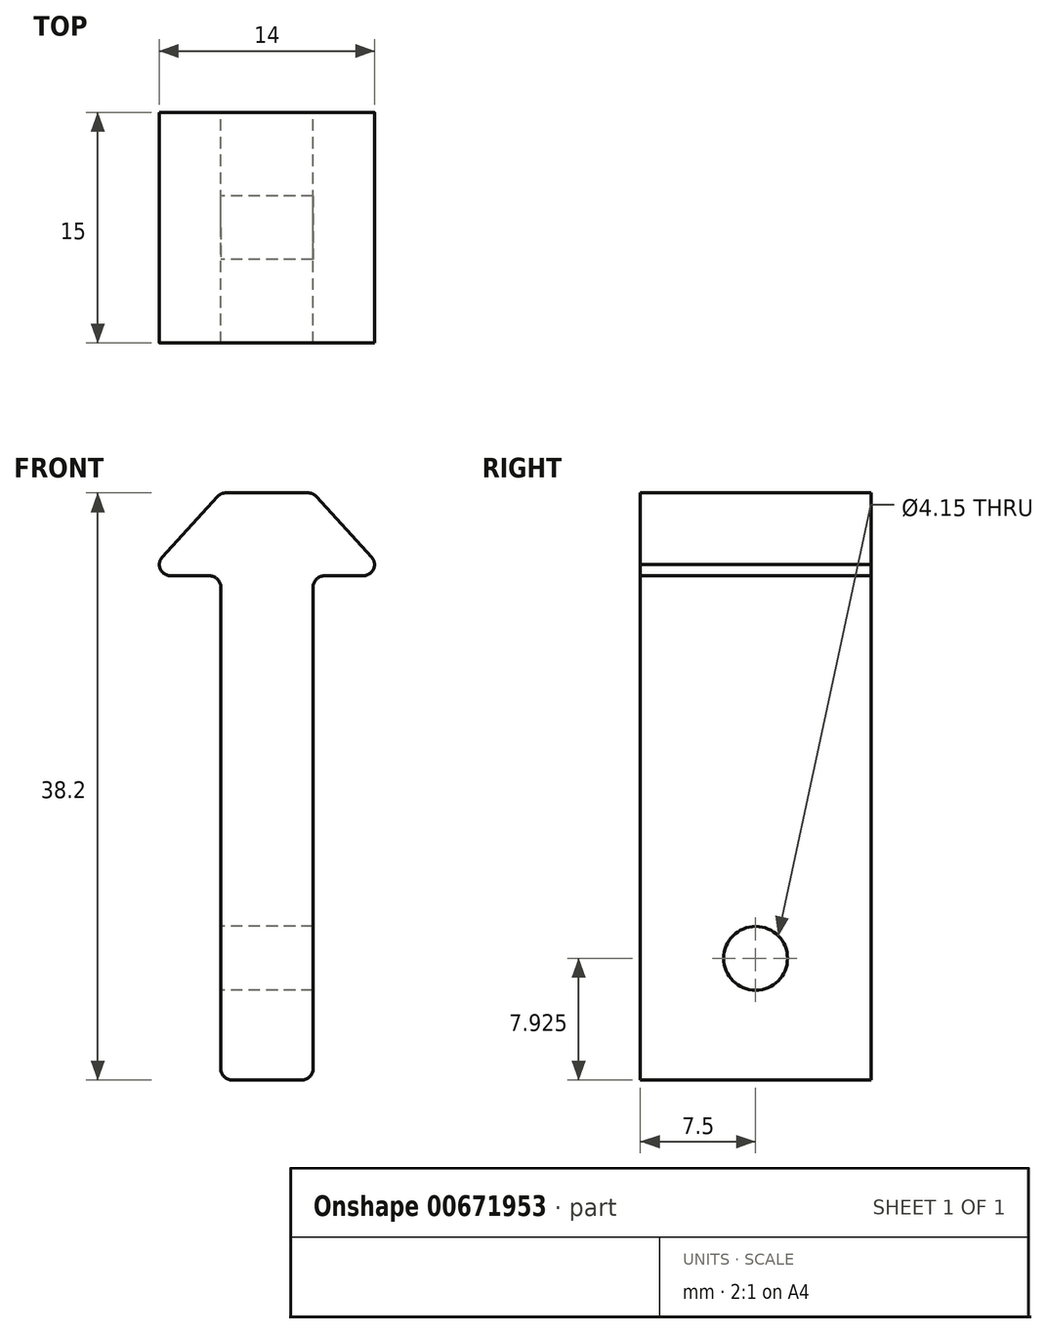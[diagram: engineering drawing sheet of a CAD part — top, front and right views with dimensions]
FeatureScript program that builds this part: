
annotation { "Feature Type Name" : "Feature", "Feature Type Description" : "" }
export const myFeature = defineFeature(function(context is Context, id is Id, definition is map)
    precondition{}
    {
        {
            var Q0;
            Q0=qCreatedBy(makeId("Front.planeOp"),FACE);
            var sketch = newSketch(context, id + "F0", { "sketchPlane" : qUnion([Q0])});
            skLineSegment(sketch, "E0", {"start": v(-3, 0) * mm, "end": v(3, 0) * mm});
            skLineSegment(sketch, "E1", {"start": v(3, 0) * mm, "end": v(3, 2.3) * mm});
            skLineSegment(sketch, "E2", {"start": v(3, 2.3) * mm, "end": v(7, 2.3) * mm});
            skLineSegment(sketch, "E3", {"start": v(7, 2.3) * mm, "end": v(7, 3.3) * mm});
            skLineSegment(sketch, "E4", {"start": v(7, 3.3) * mm, "end": v(3, 7.7) * mm});
            skLineSegment(sketch, "E5", {"start": v(3, 7.7) * mm, "end": v(-3, 7.7) * mm});
            skLineSegment(sketch, "E6", {"start": v(-3, 7.7) * mm, "end": v(-7, 3.3) * mm});
            skLineSegment(sketch, "E7", {"start": v(-7, 3.3) * mm, "end": v(-7, 2.3) * mm});
            skLineSegment(sketch, "E8", {"start": v(-7, 2.3) * mm, "end": v(-3, 2.3) * mm});
            skLineSegment(sketch, "E9", {"start": v(-3, 2.3) * mm, "end": v(-3, 0) * mm});
            skLineSegment(sketch, "E10.top", {"start": v(-3, -20.5) * mm, "end": v(3, -20.5) * mm});
            skLineSegment(sketch, "E10.left", {"start": v(-3, 0) * mm, "end": v(-3, -20.5) * mm});
            skLineSegment(sketch, "E10.right", {"start": v(3, 0) * mm, "end": v(3, -20.5) * mm});
            skLineSegment(sketch, "E11.top", {"start": v(-3, -24.5) * mm, "end": v(3, -24.5) * mm});
            skLineSegment(sketch, "E11.left", {"start": v(-3, -20.5) * mm, "end": v(-3, -24.5) * mm});
            skLineSegment(sketch, "E11.right", {"start": v(3, -20.5) * mm, "end": v(3, -24.5) * mm});
            skLineSegment(sketch, "E12.top", {"start": v(-3, -30.5) * mm, "end": v(3, -30.5) * mm});
            skLineSegment(sketch, "E12.left", {"start": v(-3, -24.5) * mm, "end": v(-3, -30.5) * mm});
            skLineSegment(sketch, "E12.right", {"start": v(3, -24.5) * mm, "end": v(3, -30.5) * mm});
            skSolve(sketch);
        }
        {
            var Q0;
            Q0=makeQuery(id+"F0.imprint","IMPRINT",FACE,{"disambiguationData":[TD([[makeQuery(id+"F0.imprint","IMPRINT",EDGE,{"derivedFrom":sQuery(id+"F0.wireOp",EDGE,"E1")}),1.0]])]});
            var Q1;
            Q1=makeQuery(id+"F0.imprint","IMPRINT",FACE,{"disambiguationData":[TD([[makeQuery(id+"F0.imprint","IMPRINT",EDGE,{"derivedFrom":sQuery(id+"F0.wireOp",EDGE,"E0")}),-1.0]])]});
            var Q2;
            Q2=makeQuery(id+"F0.imprint","IMPRINT",FACE,{"disambiguationData":[TD([[makeQuery(id+"F0.imprint","IMPRINT",EDGE,{"derivedFrom":sQuery(id+"F0.wireOp",EDGE,"E10.top")}),-1.0]])]});
            var Q3;
            Q3=makeQuery(id+"F0.imprint","IMPRINT",FACE,{"disambiguationData":[TD([[makeQuery(id+"F0.imprint","IMPRINT",EDGE,{"derivedFrom":sQuery(id+"F0.wireOp",EDGE,"E11.top")}),-1.0]])]});
            extrude(context, id + "F1", {"entities" : qUnion([Q0, Q1, Q2, Q3]), "depth" : 15 * mm, "offsetDistance" : 25 * mm});
        }
        {
            var Q0;
            Q0=makeQuery(id+"F1.opExtrude","SWEPT_EDGE",EDGE,{"disambiguationData":[OSD([sQuery(id+"F0.wireOp",EDGE,"E3"),sQuery(id+"F0.wireOp",EDGE,"E4")])]});
            var Q1;
            Q1=makeQuery(id+"F1.opExtrude","SWEPT_EDGE",EDGE,{"disambiguationData":[OSD([sQuery(id+"F0.wireOp",EDGE,"E4"),sQuery(id+"F0.wireOp",EDGE,"E5")])]});
            var Q2;
            Q2=makeQuery(id+"F1.opExtrude","SWEPT_EDGE",EDGE,{"disambiguationData":[OSD([sQuery(id+"F0.wireOp",EDGE,"E5"),sQuery(id+"F0.wireOp",EDGE,"E6")])]});
            var Q3;
            Q3=makeQuery(id+"F1.opExtrude","SWEPT_EDGE",EDGE,{"disambiguationData":[OSD([sQuery(id+"F0.wireOp",EDGE,"E6"),sQuery(id+"F0.wireOp",EDGE,"E7")])]});
            var Q4;
            Q4=makeQuery(id+"F1.opExtrude","SWEPT_EDGE",EDGE,{"disambiguationData":[OSD([sQuery(id+"F0.wireOp",EDGE,"E7"),sQuery(id+"F0.wireOp",EDGE,"E8")])]});
            var Q5;
            Q5=makeQuery(id+"F1.opExtrude","SWEPT_EDGE",EDGE,{"disambiguationData":[OSD([sQuery(id+"F0.wireOp",EDGE,"E8"),sQuery(id+"F0.wireOp",EDGE,"E9")])]});
            var Q6;
            Q6=makeQuery(id+"F1.opExtrude","SWEPT_EDGE",EDGE,{"disambiguationData":[OSD([sQuery(id+"F0.wireOp",EDGE,"E2"),sQuery(id+"F0.wireOp",EDGE,"E3")])]});
            var Q7;
            Q7=makeQuery(id+"F1.opExtrude","SWEPT_EDGE",EDGE,{"disambiguationData":[OSD([sQuery(id+"F0.wireOp",EDGE,"E1"),sQuery(id+"F0.wireOp",EDGE,"E2")])]});
            var Q8;
            Q8=makeQuery(id+"F1.opExtrude","SWEPT_EDGE",EDGE,{"disambiguationData":[OSD([sQuery(id+"F0.wireOp",EDGE,"E0"),sQuery(id+"F0.wireOp",EDGE,"E1")])]});
            var Q9;
            Q9=makeQuery(id+"F1.opExtrude","SWEPT_EDGE",EDGE,{"disambiguationData":[OSD([sQuery(id+"F0.wireOp",EDGE,"E0"),sQuery(id+"F0.wireOp",EDGE,"E9")])]});
            var Q10;
            Q10=makeQuery(id+"F1.opExtrude","SWEPT_EDGE",EDGE,{"disambiguationData":[OSD([sQuery(id+"F0.wireOp",EDGE,"E12.top"),sQuery(id+"F0.wireOp",EDGE,"E12.right")])]});
            var Q11;
            Q11=makeQuery(id+"F1.opExtrude","SWEPT_EDGE",EDGE,{"disambiguationData":[OSD([sQuery(id+"F0.wireOp",EDGE,"E12.top"),sQuery(id+"F0.wireOp",EDGE,"E12.left")])]});
            fillet(context, id + "F2", {"entities" : qUnion([Q0, Q1, Q2, Q3, Q4, Q5, Q6, Q7, Q8, Q9, Q10, Q11]), "radius" : 0.75 * mm, "tangentPropagation" : true, "allowEdgeOverflow" : false});
        }
        {
            var Q0;
            Q0=qCreatedBy(makeId("Right.planeOp"),FACE);
            var sketch = newSketch(context, id + "F3", { "sketchPlane" : qUnion([Q0])});
            skCircle(sketch, "E13", {"center": v(-7.5, -22.58) * mm, "radius": 2.08 * mm});
            skLineSegment(sketch, "E14", {"start": v(-0.41, 0) * mm, "end": v(-24.45, 0) * mm});
            skSolve(sketch);
        }
        {
            var Q0;
            Q0=makeQuery(id+"F3.imprint","IMPRINT",FACE,{"disambiguationData":[TD([[makeQuery(id+"F3.imprint","IMPRINT",EDGE,{"derivedFrom":sQuery(id+"F3.wireOp",EDGE,"E13")}),1.0]])]});
            var Q1;
            Q1=sQuery(id+"F3.wireOp",EDGE,"E13");
            extrude(context, id + "F4", {"entities" : qUnion([Q0]), "operationType" : NewBodyOperationType.REMOVE, "surfaceEntities" : qUnion([Q1]), "endBound" : BoundingType.SYMMETRIC, "depth" : 25 * mm, "offsetDistance" : 25 * mm});
        }
    });
